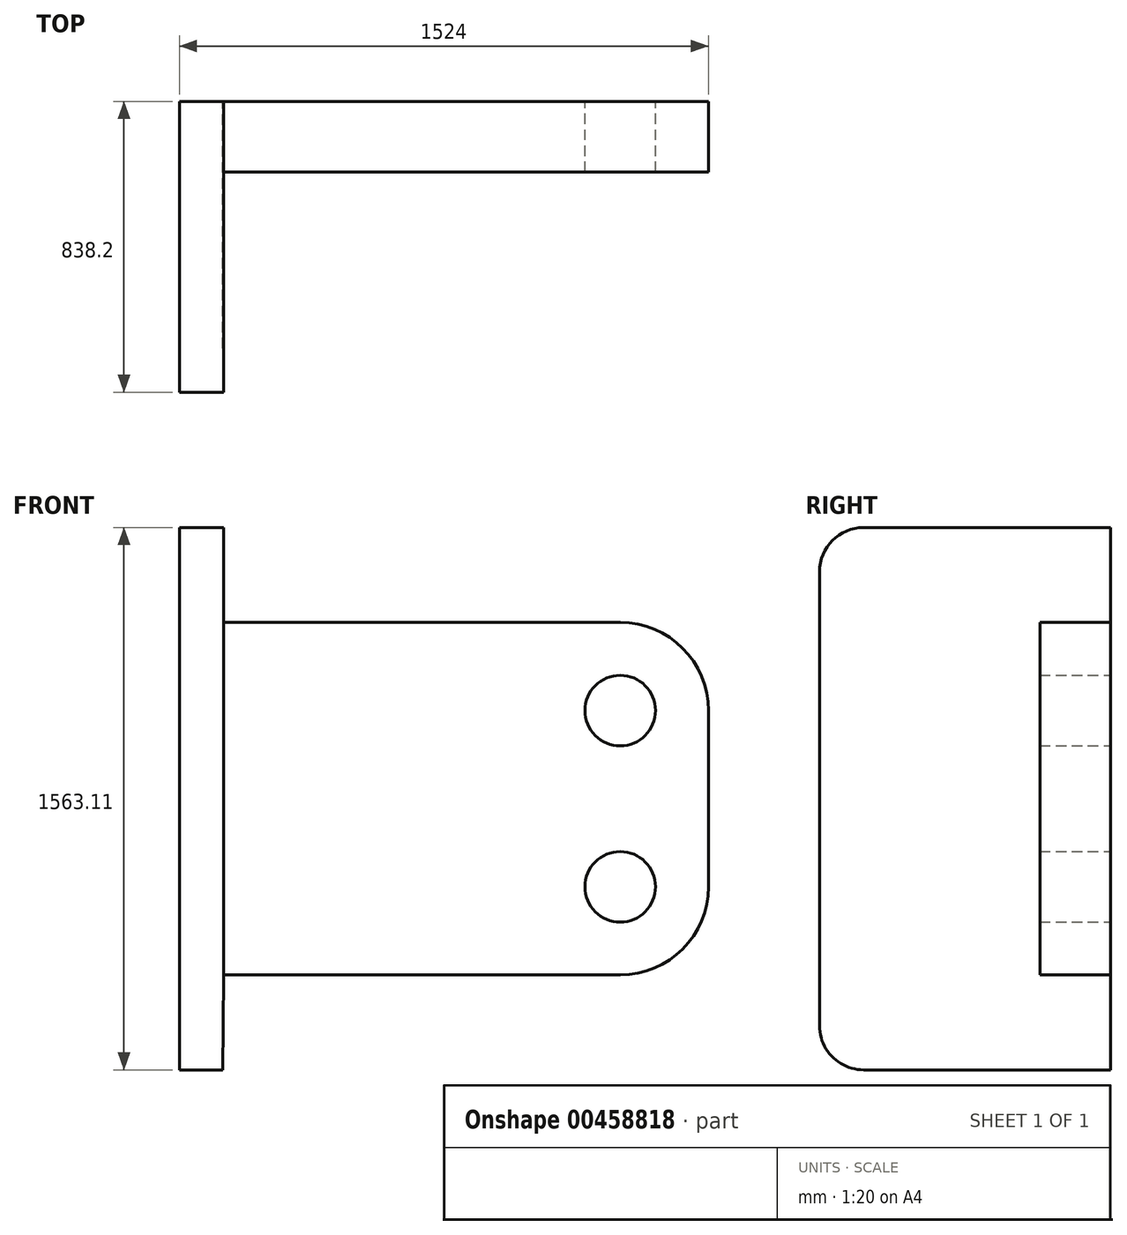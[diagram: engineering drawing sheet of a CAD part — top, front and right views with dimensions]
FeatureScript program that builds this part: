
annotation { "Feature Type Name" : "Feature", "Feature Type Description" : "" }
export const myFeature = defineFeature(function(context is Context, id is Id, definition is map)
    precondition{}
    {
        {
            var Q0;
            Q0=qCreatedBy(makeId("Front.planeOp"),FACE);
            var sketch = newSketch(context, id + "F0", { "sketchPlane" : qUnion([Q0])});
            skLineSegment(sketch, "E0", {"start": v(152.58, 204.72) * mm, "end": v(1422.58, 204.72) * mm});
            skLineSegment(sketch, "E1", {"start": v(1676.58, -49.28) * mm, "end": v(1676.58, -557.28) * mm});
            skLineSegment(sketch, "E2", {"start": v(1422.58, -811.28) * mm, "end": v(152.58, -811.28) * mm});
            skLineSegment(sketch, "E3", {"start": v(152.58, -811.28) * mm, "end": v(152.58, 204.72) * mm});
            skArc(sketch, "E4.filletArc", {"start": v(1676.58, -49.28) * mm, "mid": v(1602.18, 130.33) * mm, "end": v(1422.58, 204.72) * mm});
            skPoint(sketch, "E5.visualSharp", {"position": v(1676.58, -811.28) * mm});
            skArc(sketch, "E5.filletArc", {"start": v(1422.58, -811.28) * mm, "mid": v(1602.18, -736.88) * mm, "end": v(1676.58, -557.28) * mm});
            skLineSegment(sketch, "E6", {"start": v(1676.58, -227.08) * mm, "end": v(152.58, -227.08) * mm});
            skLineSegment(sketch, "E7", {"start": v(152.58, -379.48) * mm, "end": v(1676.58, -379.48) * mm});
            skCircle(sketch, "E8", {"center": v(1422.58, -49.28) * mm, "radius": 101.6 * mm});
            skCircle(sketch, "E9", {"center": v(1422.58, -557.28) * mm, "radius": 101.6 * mm});
            skLineSegment(sketch, "E10", {"start": v(279.58, 204.72) * mm, "end": v(279.58, -811.28) * mm});
            skLineSegment(sketch, "E11", {"start": v(152.58, 204.72) * mm, "end": v(152.58, 478.28) * mm});
            skLineSegment(sketch, "E12", {"start": v(279.58, 204.72) * mm, "end": v(279.58, 478.28) * mm});
            skLineSegment(sketch, "E13", {"start": v(279.58, 478.28) * mm, "end": v(152.58, 478.28) * mm});
            skLineSegment(sketch, "E14", {"start": v(152.58, -811.28) * mm, "end": v(152.58, -1084.83) * mm});
            skLineSegment(sketch, "E15", {"start": v(152.58, -1084.83) * mm, "end": v(277.5, -1084.83) * mm});
            skLineSegment(sketch, "E16", {"start": v(277.5, -1084.83) * mm, "end": v(279.58, -811.28) * mm});
            skSolve(sketch);
        }
        {
            var Q0;
            Q0 = qSketchRegion(id + "F0", true);
            extrude(context, id + "F1", {"entities" : qUnion([Q0]), "depth" : 203.2 * mm});
        }
        {
            var Q0;
            {var subQ0=sQuery(id+"F0.wireOp",EDGE,"E14");Q0=makeQuery(id+"F0.imprint","IMPRINT",FACE,{"disambiguationData":[TD([[makeQuery(id+"F0.imprint","IMPRINT",EDGE,{"derivedFrom":subQ0}),1.0]])]});}
            var Q1;
            {var subQ0=sQuery(id+"F0.wireOp",EDGE,"E3");var subQ5=sQuery(id+"F0.wireOp",EDGE,"E7");var subQ6=makeQuery(id+"F0.imprint","INTERSECT",VERTEX,{"derivedFrom":[subQ0,subQ5]});Q1=makeQuery(id+"F0.imprint","IMPRINT",FACE,{"disambiguationData":[TD([[makeQuery(id+"F0.imprint","IMPRINT",EDGE,{"disambiguationData":[TD([[subQ6,-1.0]])],"derivedFrom":subQ5}),-1.0]])]});}
            var Q2;
            {var subQ0=sQuery(id+"F0.wireOp",EDGE,"E6");var subQ1=sQuery(id+"F0.wireOp",EDGE,"E3");var subQ2=makeQuery(id+"F0.imprint","INTERSECT",VERTEX,{"derivedFrom":[subQ1,subQ0]});Q2=makeQuery(id+"F0.imprint","IMPRINT",FACE,{"disambiguationData":[TD([[makeQuery(id+"F0.imprint","IMPRINT",EDGE,{"disambiguationData":[TD([[subQ2,1.0]])],"derivedFrom":subQ1}),-1.0]])]});}
            var Q3;
            {var subQ0=sQuery(id+"F0.wireOp",EDGE,"E3");var subQ5=sQuery(id+"F0.wireOp",EDGE,"E6");var subQ6=makeQuery(id+"F0.imprint","INTERSECT",VERTEX,{"derivedFrom":[subQ0,subQ5]});Q3=makeQuery(id+"F0.imprint","IMPRINT",FACE,{"disambiguationData":[TD([[makeQuery(id+"F0.imprint","IMPRINT",EDGE,{"disambiguationData":[TD([[subQ6,1.0]])],"derivedFrom":subQ5}),-1.0]])]});}
            var Q4;
            {var subQ0=sQuery(id+"F0.wireOp",EDGE,"E11");Q4=makeQuery(id+"F0.imprint","IMPRINT",FACE,{"disambiguationData":[TD([[makeQuery(id+"F0.imprint","IMPRINT",EDGE,{"derivedFrom":subQ0}),-1.0]])]});}
            extrude(context, id + "F2", {"entities" : qUnion([Q0, Q1, Q2, Q3, Q4]), "operationType" : NewBodyOperationType.ADD, "depth" : 838.2 * mm});
        }
        {
            var Q0;
            {var subQ0=sQuery(id+"F0.wireOp",EDGE,"E14");var subQ1=sQuery(id+"F0.wireOp",EDGE,"E11");var subQ2=sQuery(id+"F0.wireOp",EDGE,"E3");Q0=makeQuery(id+"F2.boolean.opBoolean","MERGE",FACE,{"derivedFrom":[makeQuery(id+"F1.opExtrude","SWEPT_FACE",FACE,{"disambiguationData":[OSD([subQ2,subQ1,subQ0])]}),makeQuery(id+"F2.opExtrude","SWEPT_FACE",FACE,{"disambiguationData":[OSD([subQ2,subQ1,subQ0])]})]});}
            var sketch = newSketch(context, id + "F3", { "sketchPlane" : qUnion([Q0])});
            skLineSegment(sketch, "E17", {"start": v(0, -303.28) * mm, "end": v(838.2, -303.28) * mm, "construction": true});
            skLineSegment(sketch, "E18", {"start": v(0, 204.72) * mm, "end": v(117, 204.72) * mm});
            skCircle(sketch, "E19", {"center": v(711.2, 351.28) * mm, "radius": 127 * mm});
            skCircle(sketch, "E20", {"center": v(711.2, 351.28) * mm, "radius": 50.8 * mm});
            skLineSegment(sketch, "E21", {"start": v(117, 204.72) * mm, "end": v(117, -303.28) * mm});
            skLineSegment(sketch, "E22", {"start": v(117, 204.72) * mm, "end": v(655.86, 465.6) * mm});
            skLineSegment(sketch, "E23", {"start": v(596.9, 295.94) * mm, "end": v(244, 125.1) * mm});
            skLineSegment(sketch, "E24", {"start": v(244, 125.1) * mm, "end": v(244, -100.08) * mm});
            skLineSegment(sketch, "E25", {"start": v(244, -227.08) * mm, "end": v(711.2, -227.08) * mm});
            skLineSegment(sketch, "E26", {"start": v(244, -227.08) * mm, "end": v(117, -227.08) * mm});
            skLineSegment(sketch, "E27", {"start": v(711.2, 224.28) * mm, "end": v(711.2, -100.08) * mm});
            skLineSegment(sketch, "E28", {"start": v(711.2, -100.08) * mm, "end": v(244, -100.08) * mm});
            skLineSegment(sketch, "E29", {"start": v(711.2, -227.08) * mm, "end": v(711.2, -303.28) * mm});
            skCircle(sketch, "E30.MirrorC", {"center": v(711.2, -957.83) * mm, "radius": 127 * mm});
            skCircle(sketch, "E31.MirrorC", {"center": v(711.2, -957.83) * mm, "radius": 50.8 * mm});
            skLineSegment(sketch, "E32.MirrorCS", {"start": v(117, -811.28) * mm, "end": v(655.86, -1072.14) * mm});
            skLineSegment(sketch, "E33.MirrorCS", {"start": v(596.9, -902.5) * mm, "end": v(244, -731.66) * mm});
            skLineSegment(sketch, "E34.MirrorCS", {"start": v(711.2, -506.48) * mm, "end": v(244, -506.48) * mm});
            skLineSegment(sketch, "E35.MirrorCS", {"start": v(711.2, -830.83) * mm, "end": v(711.2, -506.48) * mm});
            skLineSegment(sketch, "E36.MirrorCS", {"start": v(711.2, -379.48) * mm, "end": v(711.2, -303.28) * mm});
            skLineSegment(sketch, "E37.MirrorCS", {"start": v(244, -379.48) * mm, "end": v(711.2, -379.48) * mm});
            skLineSegment(sketch, "E38.MirrorCS", {"start": v(244, -731.66) * mm, "end": v(244, -506.48) * mm});
            skLineSegment(sketch, "E39.MirrorCS", {"start": v(117, -811.28) * mm, "end": v(117, -303.28) * mm});
            skLineSegment(sketch, "E40.MirrorCS", {"start": v(0, -811.28) * mm, "end": v(117, -811.28) * mm});
            skLineSegment(sketch, "E41.MirrorCS", {"start": v(244, -379.48) * mm, "end": v(117, -379.48) * mm});
            skLineSegment(sketch, "E42", {"start": v(838.2, 351.28) * mm, "end": v(838.2, -957.83) * mm});
            skSolve(sketch);
        }
        {
            var Q0;
            Q0=makeQuery(id+"F2.opExtrude","CAP_EDGE",EDGE,{"disambiguationData":[OSD([sQuery(id+"F0.wireOp",EDGE,"E13")])],"isStart":false});
            var Q1;
            Q1=makeQuery(id+"F2.opExtrude","CAP_EDGE",EDGE,{"disambiguationData":[OSD([sQuery(id+"F0.wireOp",EDGE,"E15")])],"isStart":false});
            fillet(context, id + "F4", {"entities" : qUnion([Q0, Q1]), "radius" : 127 * mm, "tangentPropagation" : true, "allowEdgeOverflow" : false});
        }
    });
